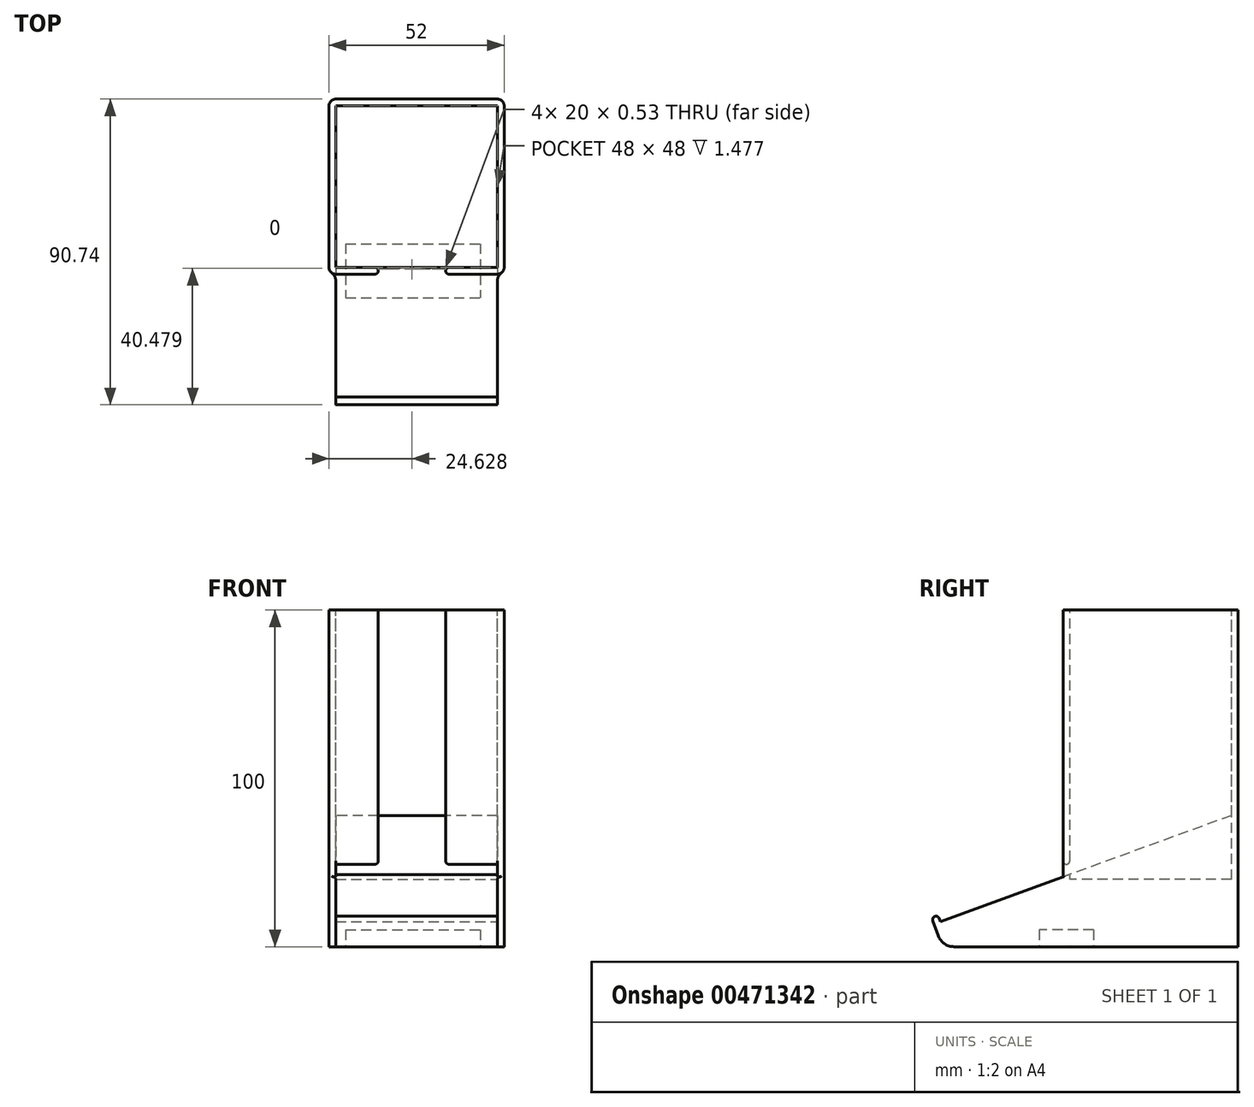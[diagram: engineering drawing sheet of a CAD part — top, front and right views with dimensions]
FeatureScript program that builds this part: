
annotation { "Feature Type Name" : "Feature", "Feature Type Description" : "" }
export const myFeature = defineFeature(function(context is Context, id is Id, definition is map)
    precondition{}
    {
        {
            var Q0;
            Q0=qCreatedBy(makeId("Top.planeOp"),FACE);
            var sketch = newSketch(context, id + "F0", { "sketchPlane" : qUnion([Q0])});
            skLineSegment(sketch, "E0.bottom", {"start": v(-48.8, 0.54) * mm, "end": v(3.2, 0.54) * mm});
            skLineSegment(sketch, "E0.top", {"start": v(-48.8, -51.46) * mm, "end": v(3.2, -51.46) * mm});
            skLineSegment(sketch, "E0.left", {"start": v(-48.8, 0.54) * mm, "end": v(-48.8, -51.46) * mm});
            skLineSegment(sketch, "E0.right", {"start": v(3.2, 0.54) * mm, "end": v(3.2, -51.46) * mm});
            skSolve(sketch);
        }
        {
            var Q0;
            Q0=makeQuery(id+"F0.imprint","IMPRINT",FACE,{"disambiguationData":[TD([[makeQuery(id+"F0.imprint","IMPRINT",EDGE,{"derivedFrom":sQuery(id+"F0.wireOp",EDGE,"E0.bottom")}),-1.0]])]});
            extrude(context, id + "F1", {"entities" : qUnion([Q0]), "depth" : 100 * mm});
        }
        {
            var Q0;
            Q0=makeQuery(id+"F1.opExtrude","CAP_FACE",FACE,{"disambiguationData":[OSD([sQuery(id+"F0.wireOp",EDGE,"E0.bottom"),sQuery(id+"F0.wireOp",EDGE,"E0.top"),sQuery(id+"F0.wireOp",EDGE,"E0.left"),sQuery(id+"F0.wireOp",EDGE,"E0.right")])],"isStart":false});
            var sketch = newSketch(context, id + "F2", { "sketchPlane" : qUnion([Q0])});
            skLineSegment(sketch, "E1.bottom", {"start": v(-46.8, -1.46) * mm, "end": v(1.2, -1.46) * mm});
            skLineSegment(sketch, "E1.top", {"start": v(-46.8, -49.46) * mm, "end": v(1.2, -49.46) * mm});
            skLineSegment(sketch, "E1.left", {"start": v(-46.8, -1.46) * mm, "end": v(-46.8, -49.46) * mm});
            skLineSegment(sketch, "E1.right", {"start": v(1.2, -1.46) * mm, "end": v(1.2, -49.46) * mm});
            skSolve(sketch);
        }
        {
            var Q0;
            Q0=makeQuery(id+"F2.imprint","IMPRINT",FACE,{"disambiguationData":[TD([[makeQuery(id+"F2.imprint","IMPRINT",EDGE,{"derivedFrom":sQuery(id+"F2.wireOp",EDGE,"E1.bottom")}),-1.0]])]});
            extrude(context, id + "F3", {"entities" : qUnion([Q0]), "operationType" : NewBodyOperationType.REMOVE, "oppositeDirection" : true, "depth" : 80 * mm});
        }
        {
            var Q0;
            Q0=qCreatedBy(makeId("Top.planeOp"),FACE);
            var sketch = newSketch(context, id + "F4", { "sketchPlane" : qUnion([Q0])});
            skLineSegment(sketch, "E2.bottom", {"start": v(20.03, -21.37) * mm, "end": v(40.03, -21.37) * mm});
            skLineSegment(sketch, "E2.top", {"start": v(20.03, -61.37) * mm, "end": v(40.03, -61.37) * mm});
            skLineSegment(sketch, "E2.left", {"start": v(20.03, -21.37) * mm, "end": v(20.03, -61.37) * mm});
            skLineSegment(sketch, "E2.right", {"start": v(40.03, -21.37) * mm, "end": v(40.03, -61.37) * mm});
            skSolve(sketch);
        }
        {
            var Q0;
            Q0=makeQuery(id+"F4.imprint","IMPRINT",FACE,{"disambiguationData":[TD([[makeQuery(id+"F4.imprint","IMPRINT",EDGE,{"derivedFrom":sQuery(id+"F4.wireOp",EDGE,"E2.bottom")}),-1.0]])]});
            extrude(context, id + "F5", {"entities" : qUnion([Q0]), "depth" : 100 * mm});
        }
        {
            var Q0;
            Q0=makeQuery(id+"F5.opExtrude","SWEPT_BODY",BODY,{"disambiguationData":[OSD([sQuery(id+"F4.wireOp",EDGE,"E2.bottom"),sQuery(id+"F4.wireOp",EDGE,"E2.top"),sQuery(id+"F4.wireOp",EDGE,"E2.left"),sQuery(id+"F4.wireOp",EDGE,"E2.right")])]});
            transform(context, id + "F6", {"entities" : qUnion([Q0]), "transformType" : TransformType.TRANSLATION_3D, "dx" : -54.2 * mm, "dy" : 9.3 * mm, "dz" : 0 * mm, "makeCopy" : false});
        }
        {
            var Q0;
            Q0=makeQuery(id+"F5.opExtrude","SWEPT_BODY",BODY,{"disambiguationData":[OSD([sQuery(id+"F4.wireOp",EDGE,"E2.bottom"),sQuery(id+"F4.wireOp",EDGE,"E2.top"),sQuery(id+"F4.wireOp",EDGE,"E2.left"),sQuery(id+"F4.wireOp",EDGE,"E2.right")])]});
            var Q1;
            Q1=makeQuery(id+"F1.opExtrude","SWEPT_BODY",BODY,{"disambiguationData":[OSD([sQuery(id+"F0.wireOp",EDGE,"E0.bottom"),sQuery(id+"F0.wireOp",EDGE,"E0.top"),sQuery(id+"F0.wireOp",EDGE,"E0.left"),sQuery(id+"F0.wireOp",EDGE,"E0.right")])]});
            booleanBodies(context, id + "F7", {"operationType" : BooleanOperationType.SUBTRACTION, "tools" : qUnion([Q0]), "targets" : qUnion([Q1])});
        }
        {
            var Q0;
            Q0=qCreatedBy(makeId("Top.planeOp"),FACE);
            var sketch = newSketch(context, id + "F8", { "sketchPlane" : qUnion([Q0])});
            skLineSegment(sketch, "E3.bottom", {"start": v(-46.8, -12.07) * mm, "end": v(1.2, -12.07) * mm});
            skLineSegment(sketch, "E3.top", {"start": v(-46.8, -60.07) * mm, "end": v(1.2, -60.07) * mm});
            skLineSegment(sketch, "E3.left", {"start": v(-46.8, -12.07) * mm, "end": v(-46.8, -60.07) * mm});
            skLineSegment(sketch, "E3.right", {"start": v(1.2, -12.07) * mm, "end": v(1.2, -60.07) * mm});
            skSolve(sketch);
        }
        {
            var Q0;
            Q0=makeQuery(id+"F8.imprint","IMPRINT",FACE,{"disambiguationData":[TD([[makeQuery(id+"F8.imprint","IMPRINT",EDGE,{"derivedFrom":sQuery(id+"F8.wireOp",EDGE,"E3.bottom")}),-1.0]])]});
            extrude(context, id + "F9", {"entities" : qUnion([Q0]), "depth" : 4.5 * mm});
        }
        {
            var Q0;
            Q0=makeQuery(id+"F9.opExtrude","SWEPT_BODY",BODY,{"disambiguationData":[OSD([sQuery(id+"F8.wireOp",EDGE,"E3.bottom"),sQuery(id+"F8.wireOp",EDGE,"E3.top"),sQuery(id+"F8.wireOp",EDGE,"E3.left"),sQuery(id+"F8.wireOp",EDGE,"E3.right")])]});
            transform(context, id + "F10", {"entities" : qUnion([Q0]), "transformType" : TransformType.TRANSLATION_3D, "dx" : 0 * mm, "dy" : 0 * mm, "dz" : 20 * mm, "makeCopy" : false});
        }
        {
            var Q0;
            Q0=makeQuery(id+"F9.opExtrude","SWEPT_BODY",BODY,{"disambiguationData":[OSD([sQuery(id+"F8.wireOp",EDGE,"E3.bottom"),sQuery(id+"F8.wireOp",EDGE,"E3.top"),sQuery(id+"F8.wireOp",EDGE,"E3.left"),sQuery(id+"F8.wireOp",EDGE,"E3.right")])]});
            var Q1;
            Q1=makeQuery(id+"F1.opExtrude","SWEPT_BODY",BODY,{"disambiguationData":[OSD([sQuery(id+"F0.wireOp",EDGE,"E0.bottom"),sQuery(id+"F0.wireOp",EDGE,"E0.top"),sQuery(id+"F0.wireOp",EDGE,"E0.left"),sQuery(id+"F0.wireOp",EDGE,"E0.right")])]});
            booleanBodies(context, id + "F11", {"operationType" : BooleanOperationType.SUBTRACTION, "tools" : qUnion([Q0]), "targets" : qUnion([Q1])});
        }
        {
            var Q0;
            Q0=makeQuery(id+"F1.opExtrude","SWEPT_EDGE",EDGE,{"disambiguationData":[OSD([sQuery(id+"F0.wireOp",EDGE,"E0.top"),sQuery(id+"F0.wireOp",EDGE,"E0.right")])]});
            fillet(context, id + "F12", {"entities" : qUnion([Q0]), "radius" : 2 * mm, "tangentPropagation" : true, "allowEdgeOverflow" : false});
        }
        {
            var Q0;
            Q0=makeQuery(id+"F1.opExtrude","SWEPT_EDGE",EDGE,{"disambiguationData":[OSD([sQuery(id+"F0.wireOp",EDGE,"E0.top"),sQuery(id+"F0.wireOp",EDGE,"E0.left")])]});
            fillet(context, id + "F13", {"entities" : qUnion([Q0]), "radius" : 2 * mm, "tangentPropagation" : true, "allowEdgeOverflow" : false});
        }
        {
            var Q0;
            Q0=makeQuery(id+"F1.opExtrude","SWEPT_EDGE",EDGE,{"disambiguationData":[OSD([sQuery(id+"F0.wireOp",EDGE,"E0.bottom"),sQuery(id+"F0.wireOp",EDGE,"E0.left")])]});
            fillet(context, id + "F14", {"entities" : qUnion([Q0]), "radius" : 2 * mm, "tangentPropagation" : true, "allowEdgeOverflow" : false});
        }
        {
            var Q0;
            Q0=makeQuery(id+"F1.opExtrude","SWEPT_EDGE",EDGE,{"disambiguationData":[OSD([sQuery(id+"F0.wireOp",EDGE,"E0.bottom"),sQuery(id+"F0.wireOp",EDGE,"E0.right")])]});
            fillet(context, id + "F15", {"entities" : qUnion([Q0]), "radius" : 2 * mm, "tangentPropagation" : true, "allowEdgeOverflow" : false});
        }
        {
            var Q0;
            {var subQ0=sQuery(id+"F0.wireOp",EDGE,"E0.top");var subQ1=makeQuery(id+"F1.opExtrude","SWEPT_FACE",FACE,{"disambiguationData":[OSD([subQ0])]});var subQ2=makeQuery(id+"F5.opExtrude","SWEPT_FACE",FACE,{"disambiguationData":[OSD([sQuery(id+"F4.wireOp",EDGE,"E2.left")])]});Q0=makeQuery(id+"F11.opBoolean","SPLIT",EDGE,{"disambiguationData":[TD([makeQuery(id+"F1.opExtrude","CAP_FACE",FACE,{"disambiguationData":[OSD([sQuery(id+"F0.wireOp",EDGE,"E0.bottom"),subQ0,sQuery(id+"F0.wireOp",EDGE,"E0.left"),sQuery(id+"F0.wireOp",EDGE,"E0.right")])],"isStart":false})])],"derivedFrom":makeQuery(id+"F7.opBoolean","INTERSECT",EDGE,{"derivedFrom":[subQ1,subQ2]})});}
            fillet(context, id + "F16", {"entities" : qUnion([Q0]), "radius" : 1 * mm, "tangentPropagation" : true, "allowEdgeOverflow" : false});
        }
        {
            var Q0;
            Q0=makeQuery(id+"F7.opBoolean","INTERSECT",EDGE,{"derivedFrom":[makeQuery(id+"F3.boolean.opBoolean","COPY",FACE,{"derivedFrom":makeQuery(id+"F3.opExtrude","SWEPT_FACE",FACE,{"disambiguationData":[OSD([sQuery(id+"F2.wireOp",EDGE,"E1.top")])]})}),makeQuery(id+"F5.opExtrude","SWEPT_FACE",FACE,{"disambiguationData":[OSD([sQuery(id+"F4.wireOp",EDGE,"E2.left")])]})]});
            fillet(context, id + "F17", {"entities" : qUnion([Q0]), "radius" : 1 * mm, "tangentPropagation" : true, "allowEdgeOverflow" : false});
        }
        {
            var Q0;
            {var subQ0=sQuery(id+"F0.wireOp",EDGE,"E0.top");var subQ1=makeQuery(id+"F1.opExtrude","SWEPT_FACE",FACE,{"disambiguationData":[OSD([subQ0])]});var subQ2=makeQuery(id+"F5.opExtrude","SWEPT_FACE",FACE,{"disambiguationData":[OSD([sQuery(id+"F4.wireOp",EDGE,"E2.right")])]});Q0=makeQuery(id+"F11.opBoolean","SPLIT",EDGE,{"disambiguationData":[TD([makeQuery(id+"F1.opExtrude","CAP_FACE",FACE,{"disambiguationData":[OSD([sQuery(id+"F0.wireOp",EDGE,"E0.bottom"),subQ0,sQuery(id+"F0.wireOp",EDGE,"E0.left"),sQuery(id+"F0.wireOp",EDGE,"E0.right")])],"isStart":false})])],"derivedFrom":makeQuery(id+"F7.opBoolean","INTERSECT",EDGE,{"derivedFrom":[subQ1,subQ2]})});}
            fillet(context, id + "F18", {"entities" : qUnion([Q0]), "radius" : 1 * mm, "tangentPropagation" : true, "allowEdgeOverflow" : false});
        }
        {
            var Q0;
            Q0=makeQuery(id+"F7.opBoolean","INTERSECT",EDGE,{"derivedFrom":[makeQuery(id+"F3.boolean.opBoolean","COPY",FACE,{"derivedFrom":makeQuery(id+"F3.opExtrude","SWEPT_FACE",FACE,{"disambiguationData":[OSD([sQuery(id+"F2.wireOp",EDGE,"E1.top")])]})}),makeQuery(id+"F5.opExtrude","SWEPT_FACE",FACE,{"disambiguationData":[OSD([sQuery(id+"F4.wireOp",EDGE,"E2.right")])]})]});
            fillet(context, id + "F19", {"entities" : qUnion([Q0]), "radius" : 1 * mm, "tangentPropagation" : true, "allowEdgeOverflow" : false});
        }
        {
            var Q0;
            Q0=qCreatedBy(makeId("Top.planeOp"),FACE);
            var sketch = newSketch(context, id + "F20", { "sketchPlane" : qUnion([Q0])});
            skLineSegment(sketch, "E4.bottom", {"start": v(-46.8, -1.46) * mm, "end": v(1.2, -1.46) * mm});
            skLineSegment(sketch, "E4.top", {"start": v(-46.8, -97.46) * mm, "end": v(1.2, -97.46) * mm});
            skLineSegment(sketch, "E4.left", {"start": v(-46.8, -1.46) * mm, "end": v(-46.8, -97.46) * mm});
            skLineSegment(sketch, "E4.right", {"start": v(1.2, -1.46) * mm, "end": v(1.2, -97.46) * mm});
            skSolve(sketch);
        }
        {
            var Q0;
            Q0=makeQuery(id+"F20.imprint","IMPRINT",FACE,{"disambiguationData":[TD([[makeQuery(id+"F20.imprint","IMPRINT",EDGE,{"derivedFrom":sQuery(id+"F20.wireOp",EDGE,"E4.bottom")}),-1.0]])]});
            extrude(context, id + "F21", {"entities" : qUnion([Q0]), "depth" : 20 * mm});
        }
        {
            var Q0;
            Q0=makeQuery(id+"F21.opExtrude","CAP_FACE",FACE,{"disambiguationData":[OSD([sQuery(id+"F20.wireOp",EDGE,"E4.bottom"),sQuery(id+"F20.wireOp",EDGE,"E4.top"),sQuery(id+"F20.wireOp",EDGE,"E4.left"),sQuery(id+"F20.wireOp",EDGE,"E4.right")])],"isStart":false});
            var sketch = newSketch(context, id + "F22", { "sketchPlane" : qUnion([Q0])});
            skLineSegment(sketch, "E5.bottom", {"start": v(-46.8, -95.46) * mm, "end": v(1.2, -95.46) * mm});
            skLineSegment(sketch, "E5.top", {"start": v(-46.8, -97.46) * mm, "end": v(1.2, -97.46) * mm});
            skLineSegment(sketch, "E5.left", {"start": v(-46.8, -95.46) * mm, "end": v(-46.8, -97.46) * mm});
            skLineSegment(sketch, "E5.right", {"start": v(1.2, -95.46) * mm, "end": v(1.2, -97.46) * mm});
            skSolve(sketch);
        }
        {
            var Q0;
            Q0 = qSketchRegion(id + "F22", true);
            extrude(context, id + "F23", {"entities" : qUnion([Q0]), "operationType" : NewBodyOperationType.ADD, "depth" : 2 * mm});
        }
        {
            var Q0;
            Q0=makeQuery(id+"F23.opExtrude","CAP_EDGE",EDGE,{"disambiguationData":[OSD([sQuery(id+"F22.wireOp",EDGE,"E5.top")])],"isStart":false});
            fillet(context, id + "F24", {"entities" : qUnion([Q0]), "radius" : 1 * mm, "tangentPropagation" : true, "allowEdgeOverflow" : false});
        }
        {
            var Q0;
            Q0=makeQuery(id+"F23.opExtrude","CAP_EDGE",EDGE,{"disambiguationData":[OSD([sQuery(id+"F22.wireOp",EDGE,"E5.bottom")])],"isStart":false});
            fillet(context, id + "F25", {"entities" : qUnion([Q0]), "radius" : 1 * mm, "tangentPropagation" : true, "allowEdgeOverflow" : false});
        }
        {
            var Q0;
            Q0=makeQuery(id+"F21.opExtrude","SWEPT_BODY",BODY,{"disambiguationData":[OSD([sQuery(id+"F20.wireOp",EDGE,"E4.bottom"),sQuery(id+"F20.wireOp",EDGE,"E4.top"),sQuery(id+"F20.wireOp",EDGE,"E4.left"),sQuery(id+"F20.wireOp",EDGE,"E4.right")])]});
            var Q1;
            Q1=makeQuery(id+"F21.opExtrude","CAP_EDGE",EDGE,{"disambiguationData":[OSD([sQuery(id+"F20.wireOp",EDGE,"E4.top")])],"isStart":true});
            transform(context, id + "F26", {"entities" : qUnion([Q0]), "transformType" : TransformType.ROTATION, "transformAxis" : qUnion([Q1]), "angle" : 20 * degree, "makeCopy" : false});
        }
        {
            var Q0;
            Q0=makeQuery(id+"F21.opExtrude","SWEPT_BODY",BODY,{"disambiguationData":[OSD([sQuery(id+"F20.wireOp",EDGE,"E4.bottom"),sQuery(id+"F20.wireOp",EDGE,"E4.top"),sQuery(id+"F20.wireOp",EDGE,"E4.left"),sQuery(id+"F20.wireOp",EDGE,"E4.right")])]});
            transform(context, id + "F27", {"entities" : qUnion([Q0]), "transformType" : TransformType.TRANSLATION_3D, "dx" : 0 * mm, "dy" : 14.5 * mm, "dz" : -12 * mm, "makeCopy" : false});
        }
        {
            var Q0;
            Q0=qCreatedBy(makeId("Top.planeOp"),FACE);
            var sketch = newSketch(context, id + "F28", { "sketchPlane" : qUnion([Q0])});
            skLineSegment(sketch, "E6.bottom", {"start": v(1.2, -1.46) * mm, "end": v(-46.8, -1.46) * mm});
            skLineSegment(sketch, "E6.top", {"start": v(1.2, -49.46) * mm, "end": v(-46.8, -49.46) * mm});
            skLineSegment(sketch, "E6.left", {"start": v(1.2, -1.46) * mm, "end": v(1.2, -49.46) * mm});
            skLineSegment(sketch, "E6.right", {"start": v(-46.8, -1.46) * mm, "end": v(-46.8, -49.46) * mm});
            skSolve(sketch);
        }
        {
            var Q0;
            Q0=makeQuery(id+"F28.imprint","IMPRINT",FACE,{"disambiguationData":[TD([[makeQuery(id+"F28.imprint","IMPRINT",EDGE,{"derivedFrom":sQuery(id+"F28.wireOp",EDGE,"E6.bottom")}),1.0]])]});
            extrude(context, id + "F29", {"entities" : qUnion([Q0]), "depth" : 20 * mm});
        }
        {
            var Q0;
            Q0=qCreatedBy(makeId("Top.planeOp"),FACE);
            var sketch = newSketch(context, id + "F30", { "sketchPlane" : qUnion([Q0])});
            skLineSegment(sketch, "E7.bottom", {"start": v(-3.82, 60.54) * mm, "end": v(56.18, 60.54) * mm});
            skLineSegment(sketch, "E7.top", {"start": v(-3.82, 0.54) * mm, "end": v(56.18, 0.54) * mm});
            skLineSegment(sketch, "E7.left", {"start": v(-3.82, 60.54) * mm, "end": v(-3.82, 0.54) * mm});
            skLineSegment(sketch, "E7.right", {"start": v(56.18, 60.54) * mm, "end": v(56.18, 0.54) * mm});
            skSolve(sketch);
        }
        {
            var Q0;
            Q0=makeQuery(id+"F30.imprint","IMPRINT",FACE,{"disambiguationData":[TD([[makeQuery(id+"F30.imprint","IMPRINT",EDGE,{"derivedFrom":sQuery(id+"F30.wireOp",EDGE,"E7.bottom")}),-1.0]])]});
            extrude(context, id + "F31", {"entities" : qUnion([Q0]), "depth" : 60 * mm});
        }
        {
            var Q0;
            Q0=makeQuery(id+"F31.opExtrude","SWEPT_BODY",BODY,{"disambiguationData":[OSD([sQuery(id+"F30.wireOp",EDGE,"E7.bottom"),sQuery(id+"F30.wireOp",EDGE,"E7.top"),sQuery(id+"F30.wireOp",EDGE,"E7.left"),sQuery(id+"F30.wireOp",EDGE,"E7.right")])]});
            transform(context, id + "F32", {"entities" : qUnion([Q0]), "transformType" : TransformType.TRANSLATION_3D, "dx" : -47.7 * mm, "dy" : 0 * mm, "dz" : 0 * mm, "makeCopy" : false});
        }
        {
            var Q0;
            Q0=makeQuery(id+"F31.opExtrude","SWEPT_BODY",BODY,{"disambiguationData":[OSD([sQuery(id+"F30.wireOp",EDGE,"E7.bottom"),sQuery(id+"F30.wireOp",EDGE,"E7.top"),sQuery(id+"F30.wireOp",EDGE,"E7.left"),sQuery(id+"F30.wireOp",EDGE,"E7.right")])]});
            transform(context, id + "F33", {"entities" : qUnion([Q0]), "transformType" : TransformType.TRANSLATION_3D, "dx" : 82.6 * mm, "dy" : 0 * mm, "dz" : 0 * mm, "makeCopy" : true});
        }
        {
            var Q0;
            Q0=makeQuery(id+"F1.opExtrude","SWEPT_BODY",BODY,{"disambiguationData":[OSD([sQuery(id+"F0.wireOp",EDGE,"E0.bottom"),sQuery(id+"F0.wireOp",EDGE,"E0.top"),sQuery(id+"F0.wireOp",EDGE,"E0.left"),sQuery(id+"F0.wireOp",EDGE,"E0.right")])]});
            var Q1;
            Q1=makeQuery(id+"F21.opExtrude","SWEPT_BODY",BODY,{"disambiguationData":[OSD([sQuery(id+"F20.wireOp",EDGE,"E4.bottom"),sQuery(id+"F20.wireOp",EDGE,"E4.top"),sQuery(id+"F20.wireOp",EDGE,"E4.left"),sQuery(id+"F20.wireOp",EDGE,"E4.right")])]});
            var Q2;
            Q2=makeQuery(id+"F29.opExtrude","SWEPT_BODY",BODY,{"disambiguationData":[OSD([sQuery(id+"F28.wireOp",EDGE,"E6.bottom"),sQuery(id+"F28.wireOp",EDGE,"E6.top"),sQuery(id+"F28.wireOp",EDGE,"E6.left"),sQuery(id+"F28.wireOp",EDGE,"E6.right")])]});
            booleanBodies(context, id + "F34", {"operationType" : BooleanOperationType.UNION, "tools" : qUnion([Q0, Q1, Q2])});
        }
        {
            var Q0;
            Q0=makeQuery(id+"F31.opExtrude","SWEPT_BODY",BODY,{"disambiguationData":[OSD([sQuery(id+"F30.wireOp",EDGE,"E7.bottom"),sQuery(id+"F30.wireOp",EDGE,"E7.top"),sQuery(id+"F30.wireOp",EDGE,"E7.left"),sQuery(id+"F30.wireOp",EDGE,"E7.right")])]});
            var Q1;
            Q1=makeQuery(id+"F1.opExtrude","SWEPT_BODY",BODY,{"disambiguationData":[OSD([sQuery(id+"F0.wireOp",EDGE,"E0.bottom"),sQuery(id+"F0.wireOp",EDGE,"E0.top"),sQuery(id+"F0.wireOp",EDGE,"E0.left"),sQuery(id+"F0.wireOp",EDGE,"E0.right")])]});
            booleanBodies(context, id + "F35", {"operationType" : BooleanOperationType.SUBTRACTION, "tools" : qUnion([Q0]), "targets" : qUnion([Q1])});
        }
        {
            var Q0;
            Q0=makeQuery(id+"F33.opPattern","COPY",BODY,{"derivedFrom":makeQuery(id+"F31.opExtrude","SWEPT_BODY",BODY,{"disambiguationData":[OSD([sQuery(id+"F30.wireOp",EDGE,"E7.bottom"),sQuery(id+"F30.wireOp",EDGE,"E7.top"),sQuery(id+"F30.wireOp",EDGE,"E7.left"),sQuery(id+"F30.wireOp",EDGE,"E7.right")])]}),"instanceName":"1"});
            deleteBodies(context, id + "F36", {"entities" : qUnion([Q0])});
        }
        {
            var Q0;
            Q0=qCreatedBy(makeId("Top.planeOp"),FACE);
            var sketch = newSketch(context, id + "F37", { "sketchPlane" : qUnion([Q0])});
            skLineSegment(sketch, "E8.bottom", {"start": v(-48.8, 30.9) * mm, "end": v(11.2, 30.9) * mm});
            skLineSegment(sketch, "E8.top", {"start": v(-48.8, -29.1) * mm, "end": v(11.2, -29.1) * mm});
            skLineSegment(sketch, "E8.left", {"start": v(-48.8, 30.9) * mm, "end": v(-48.8, -29.1) * mm});
            skLineSegment(sketch, "E8.right", {"start": v(11.2, 30.9) * mm, "end": v(11.2, -29.1) * mm});
            skSolve(sketch);
        }
        {
            var Q0;
            Q0=makeQuery(id+"F37.imprint","IMPRINT",FACE,{"disambiguationData":[TD([[makeQuery(id+"F37.imprint","IMPRINT",EDGE,{"derivedFrom":sQuery(id+"F37.wireOp",EDGE,"E8.bottom")}),-1.0]])]});
            extrude(context, id + "F38", {"entities" : qUnion([Q0]), "depth" : -30 * mm});
        }
        {
            var Q0;
            Q0=makeQuery(id+"F38.opExtrude","SWEPT_BODY",BODY,{"disambiguationData":[OSD([sQuery(id+"F37.wireOp",EDGE,"E8.bottom"),sQuery(id+"F37.wireOp",EDGE,"E8.top"),sQuery(id+"F37.wireOp",EDGE,"E8.left"),sQuery(id+"F37.wireOp",EDGE,"E8.right")])]});
            transform(context, id + "F39", {"entities" : qUnion([Q0]), "transformType" : TransformType.TRANSLATION_3D, "dx" : 0 * mm, "dy" : -72.2 * mm, "dz" : 0 * mm, "makeCopy" : false});
        }
        {
            var Q0;
            Q0=makeQuery(id+"F38.opExtrude","SWEPT_BODY",BODY,{"disambiguationData":[OSD([sQuery(id+"F37.wireOp",EDGE,"E8.bottom"),sQuery(id+"F37.wireOp",EDGE,"E8.top"),sQuery(id+"F37.wireOp",EDGE,"E8.left"),sQuery(id+"F37.wireOp",EDGE,"E8.right")])]});
            var Q1;
            Q1=makeQuery(id+"F1.opExtrude","SWEPT_BODY",BODY,{"disambiguationData":[OSD([sQuery(id+"F0.wireOp",EDGE,"E0.bottom"),sQuery(id+"F0.wireOp",EDGE,"E0.top"),sQuery(id+"F0.wireOp",EDGE,"E0.left"),sQuery(id+"F0.wireOp",EDGE,"E0.right")])]});
            booleanBodies(context, id + "F40", {"operationType" : BooleanOperationType.SUBTRACTION, "tools" : qUnion([Q0]), "targets" : qUnion([Q1])});
        }
        {
            var Q0;
            {var subQ0=sQuery(id+"F2.wireOp",EDGE,"E1.right");var subQ1=sQuery(id+"F2.wireOp",EDGE,"E1.top");Q0=makeQuery(id+"F11.opBoolean","INTERSECT",EDGE,{"derivedFrom":[makeQuery(id+"F7.opBoolean","SPLIT",FACE,{"disambiguationData":[TD([makeQuery(id+"F3.boolean.opBoolean","COPY",FACE,{"derivedFrom":makeQuery(id+"F3.opExtrude","SWEPT_FACE",FACE,{"disambiguationData":[OSD([subQ0])]})})])],"derivedFrom":makeQuery(id+"F3.boolean.opBoolean","COPY",FACE,{"derivedFrom":makeQuery(id+"F3.opExtrude","SWEPT_FACE",FACE,{"disambiguationData":[OSD([subQ1])]})})}),makeQuery(id+"F9.opExtrude","CAP_FACE",FACE,{"disambiguationData":[OSD([sQuery(id+"F8.wireOp",EDGE,"E3.bottom"),sQuery(id+"F8.wireOp",EDGE,"E3.top"),sQuery(id+"F8.wireOp",EDGE,"E3.left"),sQuery(id+"F8.wireOp",EDGE,"E3.right")])],"isStart":false})]});}
            fillet(context, id + "F41", {"entities" : qUnion([Q0]), "radius" : 1 * mm, "tangentPropagation" : true, "allowEdgeOverflow" : false});
        }
        {
            var Q0;
            {var subQ0=sQuery(id+"F2.wireOp",EDGE,"E1.left");var subQ1=sQuery(id+"F2.wireOp",EDGE,"E1.top");Q0=makeQuery(id+"F11.opBoolean","INTERSECT",EDGE,{"derivedFrom":[makeQuery(id+"F7.opBoolean","SPLIT",FACE,{"disambiguationData":[TD([makeQuery(id+"F3.boolean.opBoolean","COPY",FACE,{"derivedFrom":makeQuery(id+"F3.opExtrude","SWEPT_FACE",FACE,{"disambiguationData":[OSD([subQ0])]})})])],"derivedFrom":makeQuery(id+"F3.boolean.opBoolean","COPY",FACE,{"derivedFrom":makeQuery(id+"F3.opExtrude","SWEPT_FACE",FACE,{"disambiguationData":[OSD([subQ1])]})})}),makeQuery(id+"F9.opExtrude","CAP_FACE",FACE,{"disambiguationData":[OSD([sQuery(id+"F8.wireOp",EDGE,"E3.bottom"),sQuery(id+"F8.wireOp",EDGE,"E3.top"),sQuery(id+"F8.wireOp",EDGE,"E3.left"),sQuery(id+"F8.wireOp",EDGE,"E3.right")])],"isStart":false})]});}
            fillet(context, id + "F42", {"entities" : qUnion([Q0]), "radius" : 1 * mm, "tangentPropagation" : true, "allowEdgeOverflow" : false});
        }
        {
            var Q0;
            Q0=qCreatedBy(makeId("Top.planeOp"),FACE);
            var sketch = newSketch(context, id + "F43", { "sketchPlane" : qUnion([Q0])});
            skLineSegment(sketch, "E9.bottom", {"start": v(23.16, -56.02) * mm, "end": v(63.16, -56.02) * mm});
            skLineSegment(sketch, "E9.top", {"start": v(23.16, -72.1) * mm, "end": v(63.16, -72.1) * mm});
            skLineSegment(sketch, "E9.left", {"start": v(23.16, -56.02) * mm, "end": v(23.16, -72.1) * mm});
            skLineSegment(sketch, "E9.right", {"start": v(63.16, -56.02) * mm, "end": v(63.16, -72.1) * mm});
            skSolve(sketch);
        }
        {
            var Q0;
            Q0=makeQuery(id+"F43.imprint","IMPRINT",FACE,{"disambiguationData":[TD([[makeQuery(id+"F43.imprint","IMPRINT",EDGE,{"derivedFrom":sQuery(id+"F43.wireOp",EDGE,"E9.bottom")}),-1.0]])]});
            extrude(context, id + "F44", {"entities" : qUnion([Q0]), "depth" : 5 * mm});
        }
        {
            var Q0;
            Q0=makeQuery(id+"F44.opExtrude","SWEPT_BODY",BODY,{"disambiguationData":[OSD([sQuery(id+"F43.wireOp",EDGE,"E9.bottom"),sQuery(id+"F43.wireOp",EDGE,"E9.top"),sQuery(id+"F43.wireOp",EDGE,"E9.left"),sQuery(id+"F43.wireOp",EDGE,"E9.right")])]});
            transform(context, id + "F45", {"entities" : qUnion([Q0]), "transformType" : TransformType.TRANSLATION_3D, "dx" : -67 * mm, "dy" : 13.6 * mm, "dz" : 0 * mm, "makeCopy" : false});
        }
        {
            var Q0;
            {var subQ1=sQuery(id+"F0.wireOp",EDGE,"E0.left");var subQ2=sQuery(id+"F0.wireOp",EDGE,"E0.top");var subQ4=makeQuery(id+"F1.opExtrude","SWEPT_EDGE",EDGE,{"disambiguationData":[OSD([subQ2,subQ1])]});Q0=makeQuery(id+"F34.opBoolean","MERGE",EDGE,{"derivedFrom":[makeQuery(id+"F13.opFillet","BLEND_EDGE",EDGE,{"blendedFrom":[subQ4,makeQuery(id+"F11.opBoolean","MERGE",FACE,{"derivedFrom":[makeQuery(id+"F3.boolean.opBoolean","COPY",FACE,{"derivedFrom":makeQuery(id+"F3.opExtrude","SWEPT_FACE",FACE,{"disambiguationData":[OSD([sQuery(id+"F2.wireOp",EDGE,"E1.left")])]})}),makeQuery(id+"F9.opExtrude","SWEPT_FACE",FACE,{"disambiguationData":[OSD([sQuery(id+"F8.wireOp",EDGE,"E3.left")])]})]})],"blendedInto":[makeQuery(id+"F11.opBoolean","MERGE",FACE,{"derivedFrom":[makeQuery(id+"F3.boolean.opBoolean","COPY",FACE,{"derivedFrom":makeQuery(id+"F3.opExtrude","SWEPT_FACE",FACE,{"disambiguationData":[OSD([sQuery(id+"F2.wireOp",EDGE,"E1.left")])]})}),makeQuery(id+"F9.opExtrude","SWEPT_FACE",FACE,{"disambiguationData":[OSD([sQuery(id+"F8.wireOp",EDGE,"E3.left")])]})]})]}),makeQuery(id+"F13.opFillet","BLEND_EDGE",EDGE,{"disambiguationData":[OD(0.0)],"blendedFrom":[subQ4,makeQuery(id+"F7.opBoolean","SPLIT",FACE,{"disambiguationData":[TD([makeQuery(id+"F1.opExtrude","SWEPT_FACE",FACE,{"disambiguationData":[OSD([subQ1])]})])],"derivedFrom":makeQuery(id+"F1.opExtrude","SWEPT_FACE",FACE,{"disambiguationData":[OSD([subQ2])]})})],"blendedInto":[makeQuery(id+"F7.opBoolean","SPLIT",FACE,{"disambiguationData":[TD([makeQuery(id+"F1.opExtrude","SWEPT_FACE",FACE,{"disambiguationData":[OSD([subQ1])]})])],"derivedFrom":makeQuery(id+"F1.opExtrude","SWEPT_FACE",FACE,{"disambiguationData":[OSD([subQ2])]})})]})]});}
            fillet(context, id + "F46", {"entities" : qUnion([Q0]), "radius" : 3 * mm, "tangentPropagation" : true, "allowEdgeOverflow" : false});
        }
        {
            var Q0;
            {var subQ0=sQuery(id+"F0.wireOp",EDGE,"E0.right");var subQ2=sQuery(id+"F0.wireOp",EDGE,"E0.top");var subQ4=makeQuery(id+"F1.opExtrude","SWEPT_EDGE",EDGE,{"disambiguationData":[OSD([subQ2,subQ0])]});Q0=makeQuery(id+"F34.opBoolean","MERGE",EDGE,{"derivedFrom":[makeQuery(id+"F12.opFillet","BLEND_EDGE",EDGE,{"blendedFrom":[subQ4,makeQuery(id+"F11.opBoolean","MERGE",FACE,{"derivedFrom":[makeQuery(id+"F3.boolean.opBoolean","COPY",FACE,{"derivedFrom":makeQuery(id+"F3.opExtrude","SWEPT_FACE",FACE,{"disambiguationData":[OSD([sQuery(id+"F2.wireOp",EDGE,"E1.right")])]})}),makeQuery(id+"F9.opExtrude","SWEPT_FACE",FACE,{"disambiguationData":[OSD([sQuery(id+"F8.wireOp",EDGE,"E3.right")])]})]})],"blendedInto":[makeQuery(id+"F11.opBoolean","MERGE",FACE,{"derivedFrom":[makeQuery(id+"F3.boolean.opBoolean","COPY",FACE,{"derivedFrom":makeQuery(id+"F3.opExtrude","SWEPT_FACE",FACE,{"disambiguationData":[OSD([sQuery(id+"F2.wireOp",EDGE,"E1.right")])]})}),makeQuery(id+"F9.opExtrude","SWEPT_FACE",FACE,{"disambiguationData":[OSD([sQuery(id+"F8.wireOp",EDGE,"E3.right")])]})]})]}),makeQuery(id+"F12.opFillet","BLEND_EDGE",EDGE,{"disambiguationData":[OD(0.0)],"blendedFrom":[subQ4,makeQuery(id+"F7.opBoolean","SPLIT",FACE,{"disambiguationData":[TD([makeQuery(id+"F1.opExtrude","SWEPT_FACE",FACE,{"disambiguationData":[OSD([subQ0])]})])],"derivedFrom":makeQuery(id+"F1.opExtrude","SWEPT_FACE",FACE,{"disambiguationData":[OSD([subQ2])]})})],"blendedInto":[makeQuery(id+"F7.opBoolean","SPLIT",FACE,{"disambiguationData":[TD([makeQuery(id+"F1.opExtrude","SWEPT_FACE",FACE,{"disambiguationData":[OSD([subQ0])]})])],"derivedFrom":makeQuery(id+"F1.opExtrude","SWEPT_FACE",FACE,{"disambiguationData":[OSD([subQ2])]})})]})]});}
            fillet(context, id + "F47", {"entities" : qUnion([Q0]), "radius" : 3 * mm, "tangentPropagation" : true, "allowEdgeOverflow" : false});
        }
        {
            var Q0;
            Q0=makeQuery(id+"F40.opBoolean","INTERSECT",EDGE,{"derivedFrom":[makeQuery(id+"F23.boolean.opBoolean","MERGE",FACE,{"derivedFrom":[makeQuery(id+"F21.opExtrude","SWEPT_FACE",FACE,{"disambiguationData":[OSD([sQuery(id+"F20.wireOp",EDGE,"E4.top")])]}),makeQuery(id+"F23.opExtrude","SWEPT_FACE",FACE,{"disambiguationData":[OSD([sQuery(id+"F22.wireOp",EDGE,"E5.top")])]})]}),makeQuery(id+"F38.opExtrude","CAP_FACE",FACE,{"disambiguationData":[OSD([sQuery(id+"F37.wireOp",EDGE,"E8.bottom"),sQuery(id+"F37.wireOp",EDGE,"E8.top"),sQuery(id+"F37.wireOp",EDGE,"E8.left"),sQuery(id+"F37.wireOp",EDGE,"E8.right")])],"isStart":true})]});
            fillet(context, id + "F48", {"entities" : qUnion([Q0]), "radius" : 5 * mm, "tangentPropagation" : true, "allowEdgeOverflow" : false});
        }
    });
